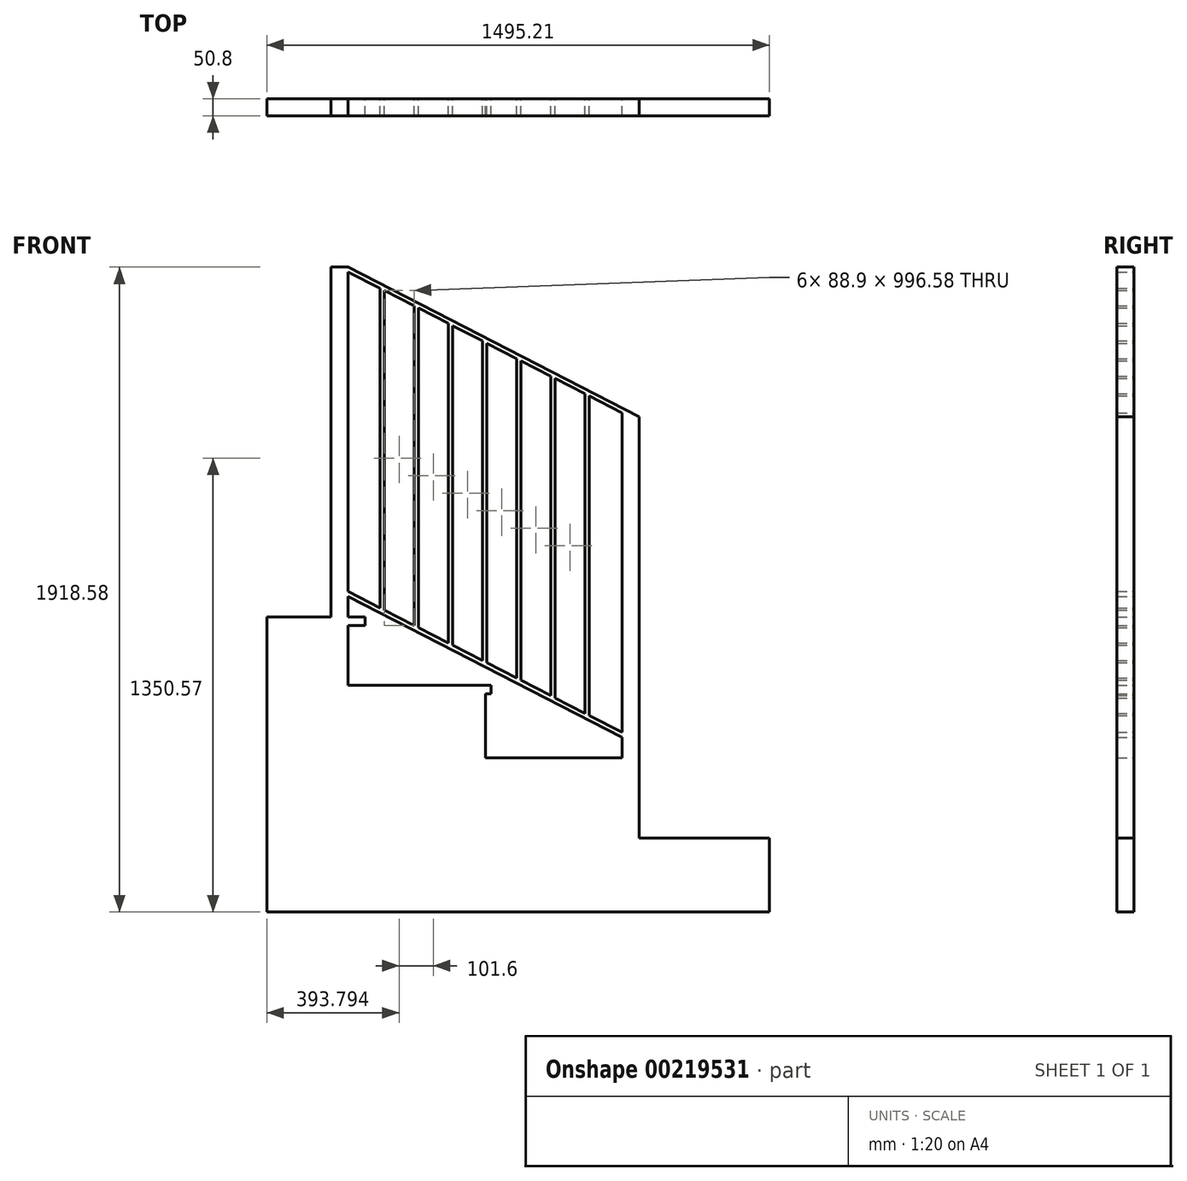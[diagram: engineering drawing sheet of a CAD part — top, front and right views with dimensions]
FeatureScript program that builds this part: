
annotation { "Feature Type Name" : "Feature", "Feature Type Description" : "" }
export const myFeature = defineFeature(function(context is Context, id is Id, definition is map)
    precondition{}
    {
        {
            var Q0;
            Q0=qCreatedBy(makeId("Front.planeOp"),FACE);
            var sketch = newSketch(context, id + "F0", { "sketchPlane" : qUnion([Q0])});
            skLineSegment(sketch, "E0", {"start": v(0, 0) * mm, "end": v(241.4, 0) * mm});
            skLineSegment(sketch, "E1", {"start": v(241.4, 0) * mm, "end": v(241.4, -203.2) * mm});
            skLineSegment(sketch, "E2", {"start": v(241.4, -203.2) * mm, "end": v(650.97, -203.2) * mm});
            skLineSegment(sketch, "E3", {"start": v(650.97, -203.2) * mm, "end": v(650.97, -419.1) * mm});
            skLineSegment(sketch, "E4", {"start": v(650.97, -419.1) * mm, "end": v(1057.37, -419.1) * mm});
            skLineSegment(sketch, "E5", {"start": v(1057.37, -419.1) * mm, "end": v(1057.37, -657.23) * mm});
            skLineSegment(sketch, "E6", {"start": v(1057.37, -657.22) * mm, "end": v(1495.21, -657.22) * mm});
            skLineSegment(sketch, "E7", {"start": v(241.4, 0) * mm, "end": v(292.2, 0) * mm});
            skLineSegment(sketch, "E8", {"start": v(292.2, 0) * mm, "end": v(292.2, -25.4) * mm});
            skLineSegment(sketch, "E9", {"start": v(292.2, -25.4) * mm, "end": v(241.4, -25.4) * mm});
            skLineSegment(sketch, "E10", {"start": v(650.97, -203.2) * mm, "end": v(666.84, -203.2) * mm});
            skLineSegment(sketch, "E11", {"start": v(666.84, -203.2) * mm, "end": v(666.84, -228.6) * mm});
            skLineSegment(sketch, "E12", {"start": v(666.84, -228.6) * mm, "end": v(650.97, -228.6) * mm});
            skLineSegment(sketch, "E13", {"start": v(1057.37, -419.1) * mm, "end": v(1076.42, -419.1) * mm});
            skLineSegment(sketch, "E14", {"start": v(1076.42, -419.1) * mm, "end": v(1076.42, -444.5) * mm});
            skLineSegment(sketch, "E15", {"start": v(1076.42, -444.5) * mm, "end": v(1057.37, -444.5) * mm});
            skLineSegment(sketch, "E16", {"start": v(241.4, 0) * mm, "end": v(241.4, 1041.4) * mm});
            skLineSegment(sketch, "E17", {"start": v(241.4, 1041.4) * mm, "end": v(190.6, 1041.4) * mm});
            skLineSegment(sketch, "E18", {"start": v(190.6, 1041.4) * mm, "end": v(190.6, 0) * mm});
            skLineSegment(sketch, "E19", {"start": v(1057.37, -419.1) * mm, "end": v(1057.37, 622.3) * mm});
            skLineSegment(sketch, "E20", {"start": v(1108.17, 596.2) * mm, "end": v(1108.17, -657.23) * mm});
            skPoint(sketch, "E21", {"position": v(241.4, 76.2) * mm});
            skPoint(sketch, "E22", {"position": v(1057.37, -342.9) * mm});
            skLineSegment(sketch, "E23", {"start": v(241.4, 76.2) * mm, "end": v(1057.37, -342.9) * mm});
            skLineSegment(sketch, "E24.0", {"start": v(241.4, 61.92) * mm, "end": v(1057.37, -357.18) * mm});
            skLineSegment(sketch, "E25", {"start": v(241.4, 1041.4) * mm, "end": v(1108.17, 596.2) * mm});
            skLineSegment(sketch, "E26.0", {"start": v(241.4, 1027.12) * mm, "end": v(1057.37, 608.02) * mm});
            skLineSegment(sketch, "E27", {"start": v(336.64, 27.28) * mm, "end": v(336.64, 978.2) * mm});
            skLineSegment(sketch, "E28.0", {"start": v(349.34, 20.75) * mm, "end": v(349.34, 971.68) * mm});
            skLineSegment(sketch, "E29.1.0.0", {"start": v(438.24, -24.9) * mm, "end": v(438.24, 926.02) * mm});
            skLineSegment(sketch, "E29.1.0.1", {"start": v(450.94, -31.43) * mm, "end": v(450.94, 919.5) * mm});
            skLineSegment(sketch, "E29.2.0.0", {"start": v(539.84, -77.09) * mm, "end": v(539.84, 873.83) * mm});
            skLineSegment(sketch, "E29.2.0.1", {"start": v(552.54, -83.61) * mm, "end": v(552.54, 867.31) * mm});
            skLineSegment(sketch, "E29.3.0.0", {"start": v(641.44, -129.27) * mm, "end": v(641.44, 821.65) * mm});
            skLineSegment(sketch, "E29.3.0.1", {"start": v(654.14, -135.8) * mm, "end": v(654.14, 815.13) * mm});
            skLineSegment(sketch, "E29.4.0.0", {"start": v(743.04, -181.46) * mm, "end": v(743.04, 769.47) * mm});
            skLineSegment(sketch, "E29.4.0.1", {"start": v(755.74, -187.98) * mm, "end": v(755.74, 762.94) * mm});
            skLineSegment(sketch, "E29.5.0.0", {"start": v(844.64, -233.64) * mm, "end": v(844.64, 717.28) * mm});
            skLineSegment(sketch, "E29.5.0.1", {"start": v(857.34, -240.16) * mm, "end": v(857.34, 710.76) * mm});
            skLineSegment(sketch, "E29.6.0.0", {"start": v(946.24, -285.82) * mm, "end": v(946.24, 665.1) * mm});
            skLineSegment(sketch, "E29.6.0.1", {"start": v(958.94, -292.35) * mm, "end": v(958.94, 658.58) * mm});
            skLineSegment(sketch, "E29.direction1", {"start": v(336.64, 27.28) * mm, "end": v(438.24, 27.28) * mm, "construction": true});
            skPoint(sketch, "E30.orphan", {"position": v(450.94, 27.28) * mm});
            skPoint(sketch, "E31.orphan", {"position": v(539.84, 27.28) * mm});
            skPoint(sketch, "E32.orphan", {"position": v(552.54, 27.28) * mm});
            skPoint(sketch, "E33.orphan", {"position": v(641.44, 27.28) * mm});
            skPoint(sketch, "E34.orphan", {"position": v(654.14, 27.28) * mm});
            skPoint(sketch, "E35.orphan", {"position": v(743.04, 27.28) * mm});
            skPoint(sketch, "E36.orphan", {"position": v(755.74, 27.28) * mm});
            skPoint(sketch, "E37.orphan", {"position": v(844.64, 27.28) * mm});
            skPoint(sketch, "E38.orphan", {"position": v(857.34, 27.28) * mm});
            skPoint(sketch, "E39.orphan", {"position": v(946.24, 27.28) * mm});
            skPoint(sketch, "E40.orphan", {"position": v(958.94, 27.28) * mm});
            skPoint(sketch, "E41.orphan", {"position": v(958.94, 978.2) * mm});
            skPoint(sketch, "E42.orphan", {"position": v(946.24, 978.2) * mm});
            skPoint(sketch, "E43.orphan", {"position": v(857.34, 978.2) * mm});
            skPoint(sketch, "E44.orphan", {"position": v(844.64, 978.2) * mm});
            skPoint(sketch, "E45.orphan", {"position": v(755.74, 978.2) * mm});
            skPoint(sketch, "E46.orphan", {"position": v(743.04, 978.2) * mm});
            skPoint(sketch, "E47.orphan", {"position": v(654.14, 978.2) * mm});
            skPoint(sketch, "E48.orphan", {"position": v(641.44, 978.2) * mm});
            skPoint(sketch, "E49.orphan", {"position": v(552.54, 978.2) * mm});
            skPoint(sketch, "E50.orphan", {"position": v(539.84, 978.2) * mm});
            skPoint(sketch, "E51.orphan", {"position": v(450.94, 978.2) * mm});
            skPoint(sketch, "E52.orphan", {"position": v(438.24, 978.2) * mm});
            skPoint(sketch, "E53.orphan", {"position": v(349.34, 978.2) * mm});
            skLineSegment(sketch, "E54", {"start": v(0, 0) * mm, "end": v(0, -877.18) * mm});
            skLineSegment(sketch, "E55", {"start": v(0, -877.18) * mm, "end": v(1495.21, -877.18) * mm});
            skLineSegment(sketch, "E56", {"start": v(1495.21, -877.18) * mm, "end": v(1495.21, -657.22) * mm});
            skPoint(sketch, "E57.orphan", {"position": v(349.34, 27.28) * mm});
            skSolve(sketch);
        }
        {
            var Q0;
            {var subQ0=sQuery(id+"F0.wireOp",EDGE,"E27");Q0=makeQuery(id+"F0.imprint","IMPRINT",FACE,{"disambiguationData":[TD([[makeQuery(id+"F0.imprint","IMPRINT",EDGE,{"derivedFrom":subQ0}),-1.0]])]});}
            var Q1;
            {var subQ0=sQuery(id+"F0.wireOp",EDGE,"E29.1.0.0");Q1=makeQuery(id+"F0.imprint","IMPRINT",FACE,{"disambiguationData":[TD([[makeQuery(id+"F0.imprint","IMPRINT",EDGE,{"derivedFrom":subQ0}),-1.0]])]});}
            var Q2;
            {var subQ0=sQuery(id+"F0.wireOp",EDGE,"E29.2.0.0");Q2=makeQuery(id+"F0.imprint","IMPRINT",FACE,{"disambiguationData":[TD([[makeQuery(id+"F0.imprint","IMPRINT",EDGE,{"derivedFrom":subQ0}),-1.0]])]});}
            var Q3;
            {var subQ0=sQuery(id+"F0.wireOp",EDGE,"E29.3.0.0");Q3=makeQuery(id+"F0.imprint","IMPRINT",FACE,{"disambiguationData":[TD([[makeQuery(id+"F0.imprint","IMPRINT",EDGE,{"derivedFrom":subQ0}),-1.0]])]});}
            var Q4;
            {var subQ0=sQuery(id+"F0.wireOp",EDGE,"E29.4.0.0");Q4=makeQuery(id+"F0.imprint","IMPRINT",FACE,{"disambiguationData":[TD([[makeQuery(id+"F0.imprint","IMPRINT",EDGE,{"derivedFrom":subQ0}),-1.0]])]});}
            var Q5;
            {var subQ0=sQuery(id+"F0.wireOp",EDGE,"E29.5.0.0");Q5=makeQuery(id+"F0.imprint","IMPRINT",FACE,{"disambiguationData":[TD([[makeQuery(id+"F0.imprint","IMPRINT",EDGE,{"derivedFrom":subQ0}),-1.0]])]});}
            var Q6;
            {var subQ0=sQuery(id+"F0.wireOp",EDGE,"E29.6.0.0");Q6=makeQuery(id+"F0.imprint","IMPRINT",FACE,{"disambiguationData":[TD([[makeQuery(id+"F0.imprint","IMPRINT",EDGE,{"derivedFrom":subQ0}),-1.0]])]});}
            var Q7;
            {var subQ6=sQuery(id+"F0.wireOp",EDGE,"E13");Q7=makeQuery(id+"F0.imprint","IMPRINT",FACE,{"disambiguationData":[TD([[makeQuery(id+"F0.imprint","IMPRINT",EDGE,{"derivedFrom":subQ6}),1.0]])]});}
            var Q8;
            {var subQ11=sQuery(id+"F0.wireOp",EDGE,"E25");var subQ12=sQuery(id+"F0.wireOp",EDGE,"E19");var subQ13=makeQuery(id+"F0.imprint","INTERSECT",VERTEX,{"derivedFrom":[subQ12,subQ11]});Q8=makeQuery(id+"F0.imprint","IMPRINT",FACE,{"disambiguationData":[TD([[makeQuery(id+"F0.imprint","IMPRINT",EDGE,{"disambiguationData":[TD([[subQ13,1.0]])],"derivedFrom":subQ12}),1.0]])]});}
            var Q9;
            {var subQ7=sQuery(id+"F0.wireOp",EDGE,"E17");Q9=makeQuery(id+"F0.imprint","IMPRINT",FACE,{"disambiguationData":[TD([[makeQuery(id+"F0.imprint","IMPRINT",EDGE,{"derivedFrom":subQ7}),1.0]])]});}
            var Q10;
            {var subQ12=sQuery(id+"F0.wireOp",EDGE,"E24.0");Q10=makeQuery(id+"F0.imprint","IMPRINT",FACE,{"disambiguationData":[TD([[makeQuery(id+"F0.imprint","IMPRINT",EDGE,{"derivedFrom":subQ12}),1.0]])]});}
            var Q11;
            {var subQ6=sQuery(id+"F0.wireOp",EDGE,"E2");Q11=makeQuery(id+"F0.imprint","IMPRINT",FACE,{"disambiguationData":[TD([[makeQuery(id+"F0.imprint","IMPRINT",EDGE,{"derivedFrom":subQ6}),-1.0]])]});}
            var Q12;
            {var subQ0=sQuery(id+"F0.wireOp",EDGE,"E10");Q12=makeQuery(id+"F0.imprint","IMPRINT",FACE,{"disambiguationData":[TD([[makeQuery(id+"F0.imprint","IMPRINT",EDGE,{"derivedFrom":subQ0}),-1.0]])]});}
            var Q13;
            {var subQ0=sQuery(id+"F0.wireOp",EDGE,"E7");Q13=makeQuery(id+"F0.imprint","IMPRINT",FACE,{"disambiguationData":[TD([[makeQuery(id+"F0.imprint","IMPRINT",EDGE,{"derivedFrom":subQ0}),-1.0]])]});}
            var Q14;
            {var subQ0=sQuery(id+"F0.wireOp",EDGE,"E13");Q14=makeQuery(id+"F0.imprint","IMPRINT",FACE,{"disambiguationData":[TD([[makeQuery(id+"F0.imprint","IMPRINT",EDGE,{"derivedFrom":subQ0}),-1.0]])]});}
            extrude(context, id + "F1", {"entities" : qUnion([Q0, Q1, Q2, Q3, Q4, Q5, Q6, Q7, Q8, Q9, Q10, Q11, Q12, Q13, Q14]), "depth" : 50.8 * mm});
        }
    });
